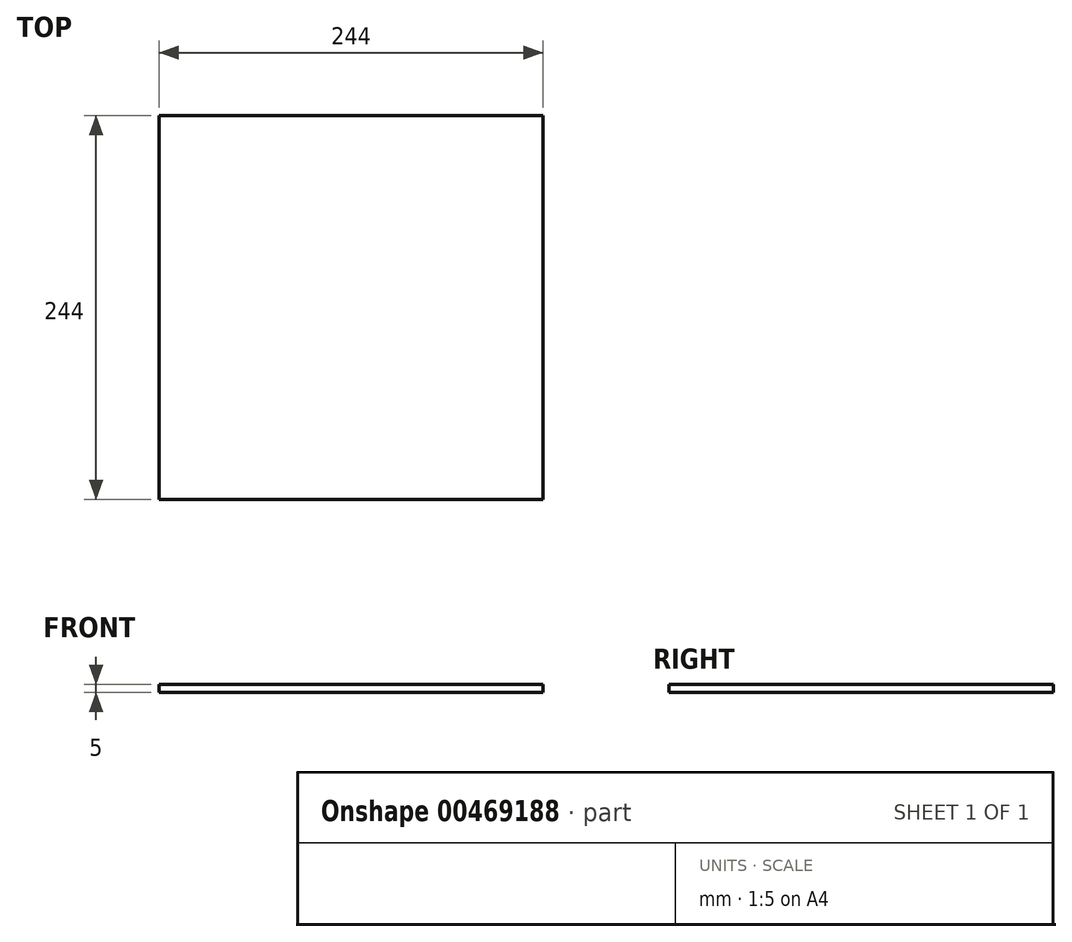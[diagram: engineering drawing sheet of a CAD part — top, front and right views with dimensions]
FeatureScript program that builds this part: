
annotation { "Feature Type Name" : "Feature", "Feature Type Description" : "" }
export const myFeature = defineFeature(function(context is Context, id is Id, definition is map)
    precondition{}
    {
        {
            var Q0;
            Q0=qCreatedBy(makeId("Top.planeOp"),FACE);
            var sketch = newSketch(context, id + "F0", { "sketchPlane" : qUnion([Q0])});
            skLineSegment(sketch, "E0.bottom", {"start": v(122, -122) * mm, "end": v(-122, -122) * mm});
            skLineSegment(sketch, "E0.top", {"start": v(122, 122) * mm, "end": v(-122, 122) * mm});
            skLineSegment(sketch, "E0.left", {"start": v(122, -122) * mm, "end": v(122, 122) * mm});
            skLineSegment(sketch, "E0.right", {"start": v(-122, -122) * mm, "end": v(-122, 122) * mm});
            skPoint(sketch, "E0.middle", {"position": v(0, 0) * mm});
            skSolve(sketch);
        }
        {
            var Q0;
            Q0 = qSketchRegion(id + "F0", true);
            extrude(context, id + "F1", {"entities" : qUnion([Q0]), "depth" : 5 * mm});
        }
    });
